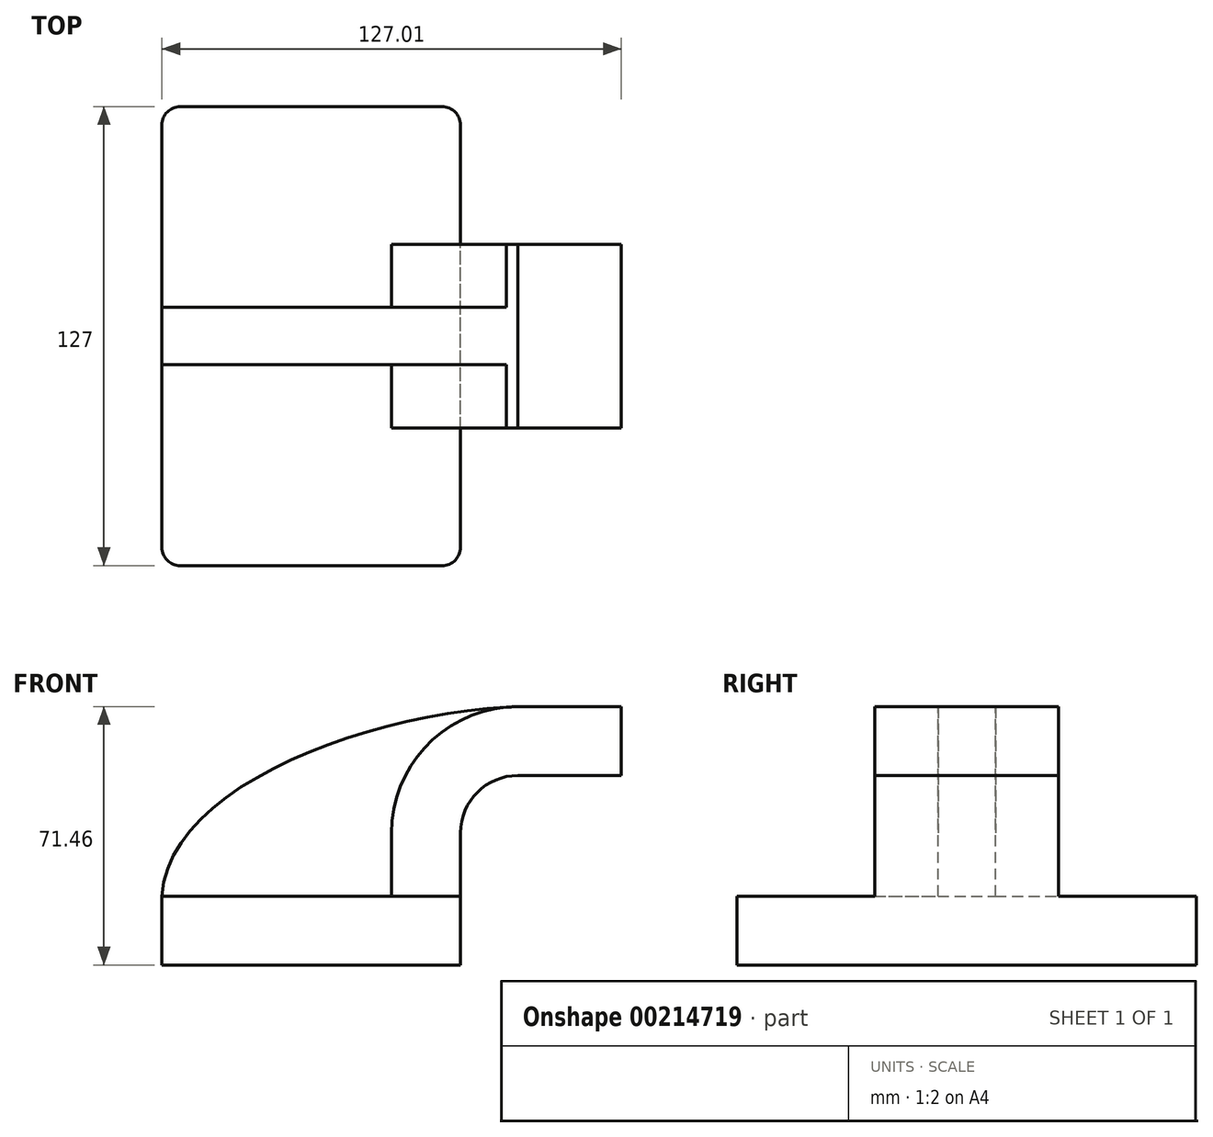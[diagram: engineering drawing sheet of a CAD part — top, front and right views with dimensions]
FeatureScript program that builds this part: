
annotation { "Feature Type Name" : "Feature", "Feature Type Description" : "" }
export const myFeature = defineFeature(function(context is Context, id is Id, definition is map)
    precondition{}
    {
        {
            var Q0;
            Q0=qCreatedBy(makeId("Front.planeOp"),FACE);
            var sketch = newSketch(context, id + "F0", { "sketchPlane" : qUnion([Q0])});
            skLineSegment(sketch, "E0.rect.bottom", {"start": v(-41.28, 9.52) * mm, "end": v(41.28, 9.52) * mm});
            skLineSegment(sketch, "E0.rect.top", {"start": v(-41.28, -9.52) * mm, "end": v(41.28, -9.52) * mm});
            skLineSegment(sketch, "E0.rect.left", {"start": v(-41.28, 9.52) * mm, "end": v(-41.28, -9.52) * mm});
            skLineSegment(sketch, "E0.rect.right", {"start": v(41.28, 9.52) * mm, "end": v(41.28, -9.52) * mm});
            skPoint(sketch, "E0.rect.middle", {"position": v(0, 0) * mm});
            skLineSegment(sketch, "E1", {"start": v(41.28, 9.52) * mm, "end": v(41.28, 27) * mm});
            skArc(sketch, "E2", {"start": v(41.28, 27) * mm, "mid": v(45.92, 38.23) * mm, "end": v(57.15, 42.88) * mm});
            skLineSegment(sketch, "E3", {"start": v(57.15, 42.88) * mm, "end": v(85.72, 42.88) * mm});
            skLineSegment(sketch, "E4.rect.bottom", {"start": v(60.32, 38.1) * mm, "end": v(111.12, 38.1) * mm});
            skLineSegment(sketch, "E4.rect.top", {"start": v(60.32, 66.68) * mm, "end": v(111.12, 66.68) * mm});
            skLineSegment(sketch, "E4.rect.left", {"start": v(60.32, 38.1) * mm, "end": v(60.32, 66.68) * mm});
            skLineSegment(sketch, "E4.rect.right", {"start": v(111.13, 38.1) * mm, "end": v(111.12, 66.68) * mm});
            skPoint(sketch, "E4.rect.middle", {"position": v(85.72, 52.39) * mm});
            skLineSegment(sketch, "E5.0", {"start": v(57.15, 61.93) * mm, "end": v(85.72, 61.93) * mm});
            skArc(sketch, "E5.1", {"start": v(22.23, 27) * mm, "mid": v(32.45, 51.7) * mm, "end": v(57.15, 61.93) * mm});
            skLineSegment(sketch, "E5.2", {"start": v(22.23, 9.52) * mm, "end": v(22.23, 27) * mm});
            skLineSegment(sketch, "E6", {"start": v(85.72, 38.1) * mm, "end": v(85.72, 66.68) * mm});
            skFitSpline(sketch, "E7", {"points": [v(-41.28, 9.53) * mm, v(57.15, 61.93) * mm], "startDerivative": vector(5.2, 92.34) * mm, "endDerivative": vector(120.92, 4.22) * mm});
            skSolve(sketch);
        }
        {
            var Q0;
            Q0=makeQuery(id+"F0.imprint","IMPRINT",FACE,{"disambiguationData":[TD([[makeQuery(id+"F0.imprint","IMPRINT",EDGE,{"derivedFrom":sQuery(id+"F0.wireOp",EDGE,"E0.rect.top")}),1.0]])]});
            extrude(context, id + "F1", {"entities" : qUnion([Q0]), "endBound" : BoundingType.SYMMETRIC, "depth" : 127 * mm});
        }
        {
            var Q0;
            {var subQ9=sQuery(id+"F0.wireOp",EDGE,"E1");Q0=makeQuery(id+"F0.imprint","IMPRINT",FACE,{"disambiguationData":[TD([[makeQuery(id+"F0.imprint","IMPRINT",EDGE,{"derivedFrom":subQ9}),1.0]])]});}
            var Q1;
            {var subQ0=sQuery(id+"F0.wireOp",EDGE,"E6");var subQ1=sQuery(id+"F0.wireOp",EDGE,"E3");var subQ2=makeQuery(id+"F0.imprint","INTERSECT",VERTEX,{"derivedFrom":[subQ1,subQ0]});Q1=makeQuery(id+"F0.imprint","IMPRINT",FACE,{"disambiguationData":[TD([[makeQuery(id+"F0.imprint","IMPRINT",EDGE,{"disambiguationData":[TD([[subQ2,1.0]])],"derivedFrom":subQ1}),1.0]])]});}
            extrude(context, id + "F2", {"entities" : qUnion([Q0, Q1]), "operationType" : NewBodyOperationType.ADD, "endBound" : BoundingType.SYMMETRIC, "depth" : 50.8 * mm});
        }
        {
            var Q0;
            {var subQ3=sQuery(id+"F0.wireOp",EDGE,"E5.2");Q0=makeQuery(id+"F0.imprint","IMPRINT",FACE,{"disambiguationData":[TD([[makeQuery(id+"F0.imprint","IMPRINT",EDGE,{"derivedFrom":subQ3}),1.0]])]});}
            extrude(context, id + "F3", {"entities" : qUnion([Q0]), "operationType" : NewBodyOperationType.ADD, "endBound" : BoundingType.SYMMETRIC, "depth" : 15.88 * mm});
        }
        {
            var Q0;
            Q0=makeQuery(id+"F1.opExtrude","CAP_EDGE",EDGE,{"disambiguationData":[OSD([sQuery(id+"F0.wireOp",EDGE,"E0.rect.right")])],"isStart":false});
            var Q1;
            Q1=makeQuery(id+"F1.opExtrude","CAP_EDGE",EDGE,{"disambiguationData":[OSD([sQuery(id+"F0.wireOp",EDGE,"E0.rect.left")])],"isStart":false});
            var Q2;
            Q2=makeQuery(id+"F1.opExtrude","CAP_EDGE",EDGE,{"disambiguationData":[OSD([sQuery(id+"F0.wireOp",EDGE,"E0.rect.right")])],"isStart":true});
            var Q3;
            Q3=makeQuery(id+"F1.opExtrude","CAP_EDGE",EDGE,{"disambiguationData":[OSD([sQuery(id+"F0.wireOp",EDGE,"E0.rect.left")])],"isStart":true});
            fillet(context, id + "F4", {"entities" : qUnion([Q0, Q1, Q2, Q3]), "radius" : 5.08 * mm, "tangentPropagation" : true, "allowEdgeOverflow" : false});
        }
    });
